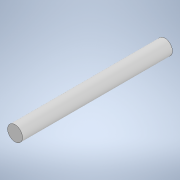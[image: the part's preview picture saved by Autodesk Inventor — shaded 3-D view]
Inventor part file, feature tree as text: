
AUTODESK INVENTOR PART (.ipt)
format: ipt  version: 2021 (Build 250183000, 183)  size: 91,648 bytes
history: native  units: mm
features: extrude x1, sketch x1
ambient origin geometry x8: Origin, YZ Plane, XZ Plane, XY Plane, X Axis, Y Axis, Z Axis, Center Point
bodies: Solid1 (feature_tree)
feature tree (2):
  extrude  "Extrusion1"  Depth=30.0mm TaperAngle=0.0deg
  sketch  "Sketch1"  dims[d0=3.0mm d1=30.0mm d2=0.0mm d4=0.5mm d5=0.872665mm d6=0.5mm d7=0.872665mm]
